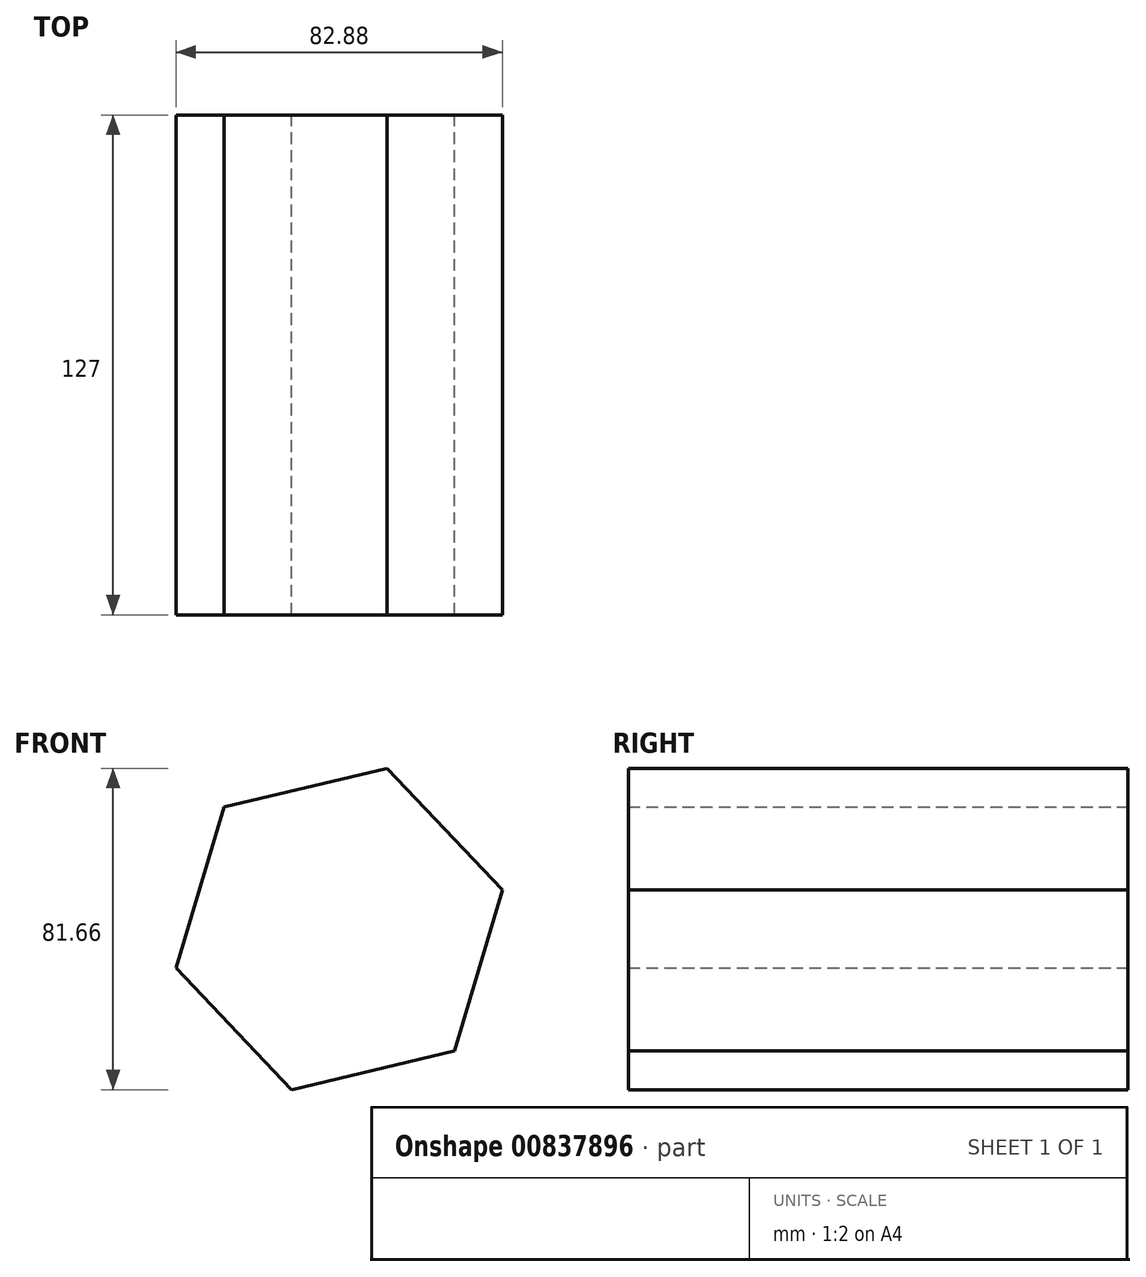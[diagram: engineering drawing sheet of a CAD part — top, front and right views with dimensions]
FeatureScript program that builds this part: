
annotation { "Feature Type Name" : "Feature", "Feature Type Description" : "" }
export const myFeature = defineFeature(function(context is Context, id is Id, definition is map)
    precondition{}
    {
        {
            var Q0;
            Q0=qCreatedBy(makeId("Front.planeOp"),FACE);
            var sketch = newSketch(context, id + "F0", { "sketchPlane" : qUnion([Q0])});
            skCircle(sketch, "E0.cCircle", {"center": v(0, 0) * mm, "radius": 67.63 * mm, "construction": true});
            skLineSegment(sketch, "E0.0", {"start": v(0, -67.63) * mm, "end": v(-58.57, -33.81) * mm});
            skLineSegment(sketch, "E0.1", {"start": v(-58.57, -33.81) * mm, "end": v(-58.57, 33.81) * mm});
            skLineSegment(sketch, "E0.2", {"start": v(-58.57, 33.81) * mm, "end": v(0, 67.63) * mm});
            skLineSegment(sketch, "E0.3", {"start": v(0, 67.63) * mm, "end": v(58.57, 33.81) * mm});
            skLineSegment(sketch, "E0.4", {"start": v(58.57, 33.81) * mm, "end": v(58.57, -33.81) * mm});
            skLineSegment(sketch, "E0.5", {"start": v(58.57, -33.81) * mm, "end": v(0, -67.63) * mm});
            skCircle(sketch, "E1.cCircle", {"center": v(29.28, -50.72) * mm, "radius": 42.6 * mm, "construction": true});
            skLineSegment(sketch, "E1.0", {"start": v(-12.16, -60.6) * mm, "end": v(0, -19.78) * mm});
            skLineSegment(sketch, "E1.1", {"start": v(0, -19.78) * mm, "end": v(41.44, -9.89) * mm});
            skLineSegment(sketch, "E1.2", {"start": v(41.44, -9.89) * mm, "end": v(70.72, -40.83) * mm});
            skLineSegment(sketch, "E1.3", {"start": v(70.72, -40.83) * mm, "end": v(58.57, -81.66) * mm});
            skLineSegment(sketch, "E1.4", {"start": v(58.57, -81.66) * mm, "end": v(17.13, -91.55) * mm});
            skLineSegment(sketch, "E1.5", {"start": v(17.13, -91.55) * mm, "end": v(-12.16, -60.6) * mm});
            skSolve(sketch);
        }
        {
            var Q0;
            {var subQ0=sQuery(id+"F0.wireOp",EDGE,"E0.5");Q0=makeQuery(id+"F0.imprint","IMPRINT",FACE,{"disambiguationData":[TD([[makeQuery(id+"F0.imprint","IMPRINT",EDGE,{"derivedFrom":subQ0}),1.0]])]});}
            var Q1;
            {var subQ1=sQuery(id+"F0.wireOp",EDGE,"E0.5");Q1=makeQuery(id+"F0.imprint","IMPRINT",FACE,{"disambiguationData":[TD([[makeQuery(id+"F0.imprint","IMPRINT",EDGE,{"derivedFrom":subQ1}),-1.0]])]});}
            extrude(context, id + "F1", {"entities" : qUnion([Q0, Q1]), "depth" : 127 * mm, "offsetDistance" : 25.4 * mm});
        }
    });
